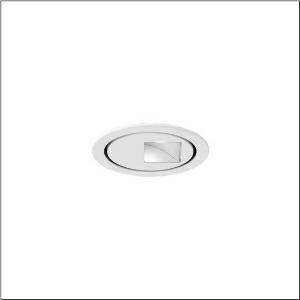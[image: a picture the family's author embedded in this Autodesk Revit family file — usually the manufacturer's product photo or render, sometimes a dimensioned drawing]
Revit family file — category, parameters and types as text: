
# Revit family: lunis_11_micro_round_51dj11cd1wf21
name_source: partatom
category: Lighting Fixtures
units: mm (PartAtom-declared; Revit-internal decimal feet)

## family parameters
Cut with Voids When Loaded = No
Host = Face
Light Source = No
Part Type = Normal
Room Calculation Point = No
Round Connector Dimension = Use Diameter
Shared = No

## types (1)
- Lunis 11 micro round (1 x LED 3000K / CRI = 80 (unbekannt), 1320 lm, 3000K)
    Apparent Load = 20 VA
    CIE Flux Codes = 42 75 96 100 100
    Color Rendering = 80
    Color Temperature = 3000K
    Default Elevation = 1800 mm
    Description = Lunis 11 micro round, downlight, light control with wallwasher, of highly reflective aluminium, highly specular, light emission: direct distribution, LED rated luminous flux: 1.320lm, light colour: 830, control gear: ECG, with terminal, 5-pole, mains connection: 220..230V, AC/DC, 0/50..60Hz, LED module, luminaire module, of aluminium, highly specular, white, diameter: 114mm, clamping range: 1..40mm, recessing ring, of plastic, traffic white (RAL 9016), protection rating (complete): IP20, insulation class (complete): insulation class II (safety insulation), certification: CE, permissible ambient temperature for indoor applications: 0..+35°C, packaging unit: 1 piece
    Height = 0 mm  [stored 0 ft]
    Lamp = 1 x LED 3000K / CRI >= 80 (unbekannt)
    Lamp Light Flux = 1320 lm
    Lamp count = 1
    Length = 114 mm
    Luminous efficacy = 67 lm/W
    Manufacturer = Siteco
    ModVariant = No
    Model = 51DJ11CD1WF21
    Mounting Place = Ceiling
    Mounting Type = Recessed
    Number of Poles = 1
    OnlyDefault = Yes
    Power Factor = 1
    Product Name = Lunis 11 micro round
    Product group = downlight | ceiling recessed
    ProductGroupID = 402
    Protection Class = Protection class II
    Protection Degree = IP 20
    RLX_Detail_Level = 1
    RlxData = <blob elided: 40089 chars, md5=bc971cda>
    Socket = socket
    Standby Power = 0 W
    System Light Flux = 1320 lm
    System Power = 20 W
    Type Comments = Product without accessories
    Type Image = l_1004773.jpg
    URL = http://relux.com
    VarID = ---
    Voltage = 0 V
    Weight = 0.00 kg
    Width = 114 mm

note: [stored X ft] marks values corroborated as IEEE doubles in the binary element streams (Revit-internal decimal feet)

## geometry (parser evidence)
native form markers: Blend x4, Sweep x10
no freeform markers — native parametric forms only
